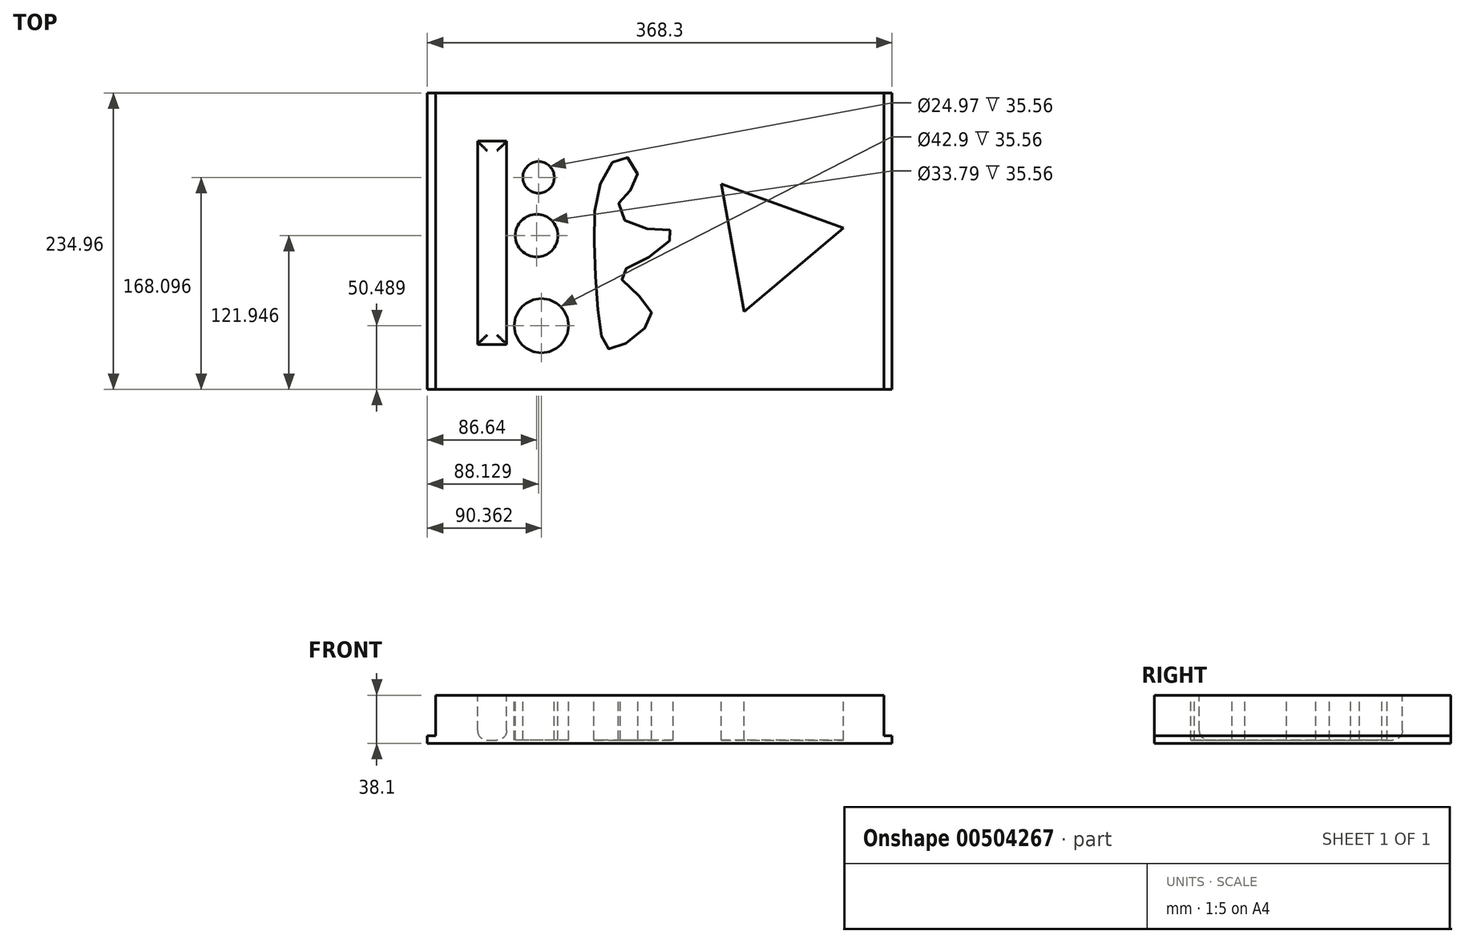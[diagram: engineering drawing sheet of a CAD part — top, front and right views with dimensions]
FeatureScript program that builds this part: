
annotation { "Feature Type Name" : "Feature", "Feature Type Description" : "" }
export const myFeature = defineFeature(function(context is Context, id is Id, definition is map)
    precondition{}
    {
        {
            var Q0;
            Q0=qCreatedBy(makeId("Top.planeOp"),FACE);
            var sketch = newSketch(context, id + "F0", { "sketchPlane" : qUnion([Q0])});
            skLineSegment(sketch, "E0.bottom", {"start": v(184.15, -117.47) * mm, "end": v(-184.15, -117.48) * mm});
            skLineSegment(sketch, "E0.top", {"start": v(184.15, 117.48) * mm, "end": v(-184.15, 117.47) * mm});
            skLineSegment(sketch, "E0.left", {"start": v(184.15, -117.47) * mm, "end": v(184.15, 117.48) * mm});
            skLineSegment(sketch, "E0.right", {"start": v(-184.15, -117.48) * mm, "end": v(-184.15, 117.47) * mm});
            skPoint(sketch, "E0.middle", {"position": v(0, 0) * mm});
            skSolve(sketch);
        }
        {
            var Q0;
            Q0=makeQuery(id+"F0.imprint","IMPRINT",FACE,{"disambiguationData":[TD([[makeQuery(id+"F0.imprint","IMPRINT",EDGE,{"derivedFrom":sQuery(id+"F0.wireOp",EDGE,"E0.bottom")}),-1.0]])]});
            extrude(context, id + "F1", {"entities" : qUnion([Q0]), "depth" : 38.1 * mm});
        }
        {
            var Q0;
            Q0=makeQuery(id+"F1.opExtrude","SWEPT_FACE",FACE,{"disambiguationData":[OSD([sQuery(id+"F0.wireOp",EDGE,"E0.bottom")])]});
            var sketch = newSketch(context, id + "F2", { "sketchPlane" : qUnion([Q0])});
            skLineSegment(sketch, "E1.bottom", {"start": v(184.15, 38.1) * mm, "end": v(177.55, 38.1) * mm});
            skLineSegment(sketch, "E1.top", {"start": v(184.15, 6.1) * mm, "end": v(177.55, 6.1) * mm});
            skLineSegment(sketch, "E1.left", {"start": v(184.15, 38.1) * mm, "end": v(184.15, 6.1) * mm});
            skLineSegment(sketch, "E1.right", {"start": v(177.55, 38.1) * mm, "end": v(177.55, 6.1) * mm});
            skLineSegment(sketch, "E2.bottom", {"start": v(-184.15, 38.1) * mm, "end": v(-177.55, 38.1) * mm});
            skLineSegment(sketch, "E2.top", {"start": v(-184.15, 6.1) * mm, "end": v(-177.55, 6.1) * mm});
            skLineSegment(sketch, "E2.left", {"start": v(-184.15, 38.1) * mm, "end": v(-184.15, 6.1) * mm});
            skLineSegment(sketch, "E2.right", {"start": v(-177.55, 38.1) * mm, "end": v(-177.55, 6.1) * mm});
            skSolve(sketch);
        }
        {
            var Q0;
            Q0=makeQuery(id+"F2.imprint","IMPRINT",FACE,{"disambiguationData":[TD([[makeQuery(id+"F2.imprint","IMPRINT",EDGE,{"derivedFrom":sQuery(id+"F2.wireOp",EDGE,"E1.bottom")}),1.0]])]});
            var Q1;
            Q1=makeQuery(id+"F2.imprint","IMPRINT",FACE,{"disambiguationData":[TD([[makeQuery(id+"F2.imprint","IMPRINT",EDGE,{"derivedFrom":sQuery(id+"F2.wireOp",EDGE,"E2.bottom")}),1.0]])]});
            extrude(context, id + "F3", {"entities" : qUnion([Q0, Q1]), "operationType" : NewBodyOperationType.REMOVE, "endBound" : BoundingType.THROUGH_ALL, "oppositeDirection" : true, "depth" : 25.4 * mm});
        }
        {
            var Q0;
            Q0=makeQuery(id+"F1.opExtrude","CAP_FACE",FACE,{"disambiguationData":[OSD([sQuery(id+"F0.wireOp",EDGE,"E0.bottom"),sQuery(id+"F0.wireOp",EDGE,"E0.top"),sQuery(id+"F0.wireOp",EDGE,"E0.left"),sQuery(id+"F0.wireOp",EDGE,"E0.right")])],"isStart":false});
            var sketch = newSketch(context, id + "F4", { "sketchPlane" : qUnion([Q0])});
            skLineSegment(sketch, "E3.bottom", {"start": v(-144.4, -81.88) * mm, "end": v(-121.33, -81.88) * mm});
            skLineSegment(sketch, "E3.top", {"start": v(-144.4, 79.27) * mm, "end": v(-121.33, 79.27) * mm});
            skLineSegment(sketch, "E3.left", {"start": v(-144.4, -81.88) * mm, "end": v(-144.4, 79.27) * mm});
            skLineSegment(sketch, "E3.right", {"start": v(-121.33, -81.88) * mm, "end": v(-121.33, 79.27) * mm});
            skCircle(sketch, "E4", {"center": v(-93.79, -67) * mm, "radius": 21.45 * mm});
            skCircle(sketch, "E5", {"center": v(-105.33, -35.36) * mm, "radius": 7.34 * mm});
            skCircle(sketch, "E6", {"center": v(-90.44, -27.91) * mm, "radius": 6.6 * mm});
            skCircle(sketch, "E7", {"center": v(-97.5, 4.47) * mm, "radius": 16.9 * mm});
            skCircle(sketch, "E8", {"center": v(-96.02, 50.62) * mm, "radius": 12.48 * mm});
            skCircle(sketch, "E9", {"center": v(-105.33, 74.06) * mm, "radius": 8.5 * mm});
            skFitSpline(sketch, "E10", {"points": [v(-46.15, -75.18) * mm, v(-51.73, -9.68) * mm, v(-45.78, 48.75) * mm, v(-27.17, 67) * mm, v(-17.86, 47.64) * mm, v(-32, 31.26) * mm, v(-21.21, 12.28) * mm, v(10.42, 7.44) * mm, v(-10.05, -13.4) * mm, v(-31.26, -27.54) * mm, v(-8.56, -51.73) * mm, v(-11.17, -68.1) * mm, v(-38.7, -85.6) * mm, v(-46.15, -75.18) * mm]});
            skCircle(sketch, "E11.cCircle", {"center": v(87.09, 0) * mm, "radius": 29.67 * mm, "construction": true});
            skLineSegment(sketch, "E11.0", {"start": v(48.8, 45.32) * mm, "end": v(145.48, 10.5) * mm});
            skLineSegment(sketch, "E11.1", {"start": v(145.48, 10.5) * mm, "end": v(67, -55.83) * mm});
            skLineSegment(sketch, "E11.2", {"start": v(67, -55.83) * mm, "end": v(48.8, 45.32) * mm});
            skPoint(sketch, "E11.0.midPoint", {"position": v(97.14, 27.91) * mm});
            skSolve(sketch);
        }
        {
            var Q0;
            Q0=makeQuery(id+"F4.imprint","IMPRINT",FACE,{"disambiguationData":[TD([[makeQuery(id+"F4.imprint","IMPRINT",EDGE,{"derivedFrom":sQuery(id+"F4.wireOp",EDGE,"E10")}),-1.0]])]});
            var Q1;
            Q1=makeQuery(id+"F4.imprint","IMPRINT",FACE,{"disambiguationData":[TD([[makeQuery(id+"F4.imprint","IMPRINT",EDGE,{"derivedFrom":sQuery(id+"F4.wireOp",EDGE,"E7")}),1.0]])]});
            var Q2;
            Q2=makeQuery(id+"F4.imprint","IMPRINT",FACE,{"disambiguationData":[TD([[makeQuery(id+"F4.imprint","IMPRINT",EDGE,{"derivedFrom":sQuery(id+"F4.wireOp",EDGE,"E4")}),1.0]])]});
            var Q3;
            Q3=makeQuery(id+"F4.imprint","IMPRINT",FACE,{"disambiguationData":[TD([[makeQuery(id+"F4.imprint","IMPRINT",EDGE,{"derivedFrom":sQuery(id+"F4.wireOp",EDGE,"E3.bottom")}),1.0]])]});
            var Q4;
            Q4=makeQuery(id+"F4.imprint","IMPRINT",FACE,{"disambiguationData":[TD([[makeQuery(id+"F4.imprint","IMPRINT",EDGE,{"derivedFrom":sQuery(id+"F4.wireOp",EDGE,"E8")}),1.0]])]});
            var Q5;
            Q5=makeQuery(id+"F4.imprint","IMPRINT",FACE,{"disambiguationData":[TD([[makeQuery(id+"F4.imprint","IMPRINT",EDGE,{"derivedFrom":sQuery(id+"F4.wireOp",EDGE,"E11.0")}),-1.0]])]});
            extrude(context, id + "F5", {"entities" : qUnion([Q0, Q1, Q2, Q3, Q4, Q5]), "operationType" : NewBodyOperationType.REMOVE, "oppositeDirection" : true, "depth" : 35.56 * mm});
        }
        {
            var Q0;
            Q0=makeQuery(id+"F5.boolean.opBoolean","COPY",FACE,{"derivedFrom":makeQuery(id+"F5.opExtrude","CAP_FACE",FACE,{"disambiguationData":[OSD([sQuery(id+"F4.wireOp",EDGE,"E3.bottom"),sQuery(id+"F4.wireOp",EDGE,"E3.top"),sQuery(id+"F4.wireOp",EDGE,"E3.left"),sQuery(id+"F4.wireOp",EDGE,"E3.right")])],"isStart":false})});
            fillet(context, id + "F6", {"entities" : qUnion([Q0]), "radius" : 7.62 * mm, "tangentPropagation" : true, "allowEdgeOverflow" : false});
        }
    });
